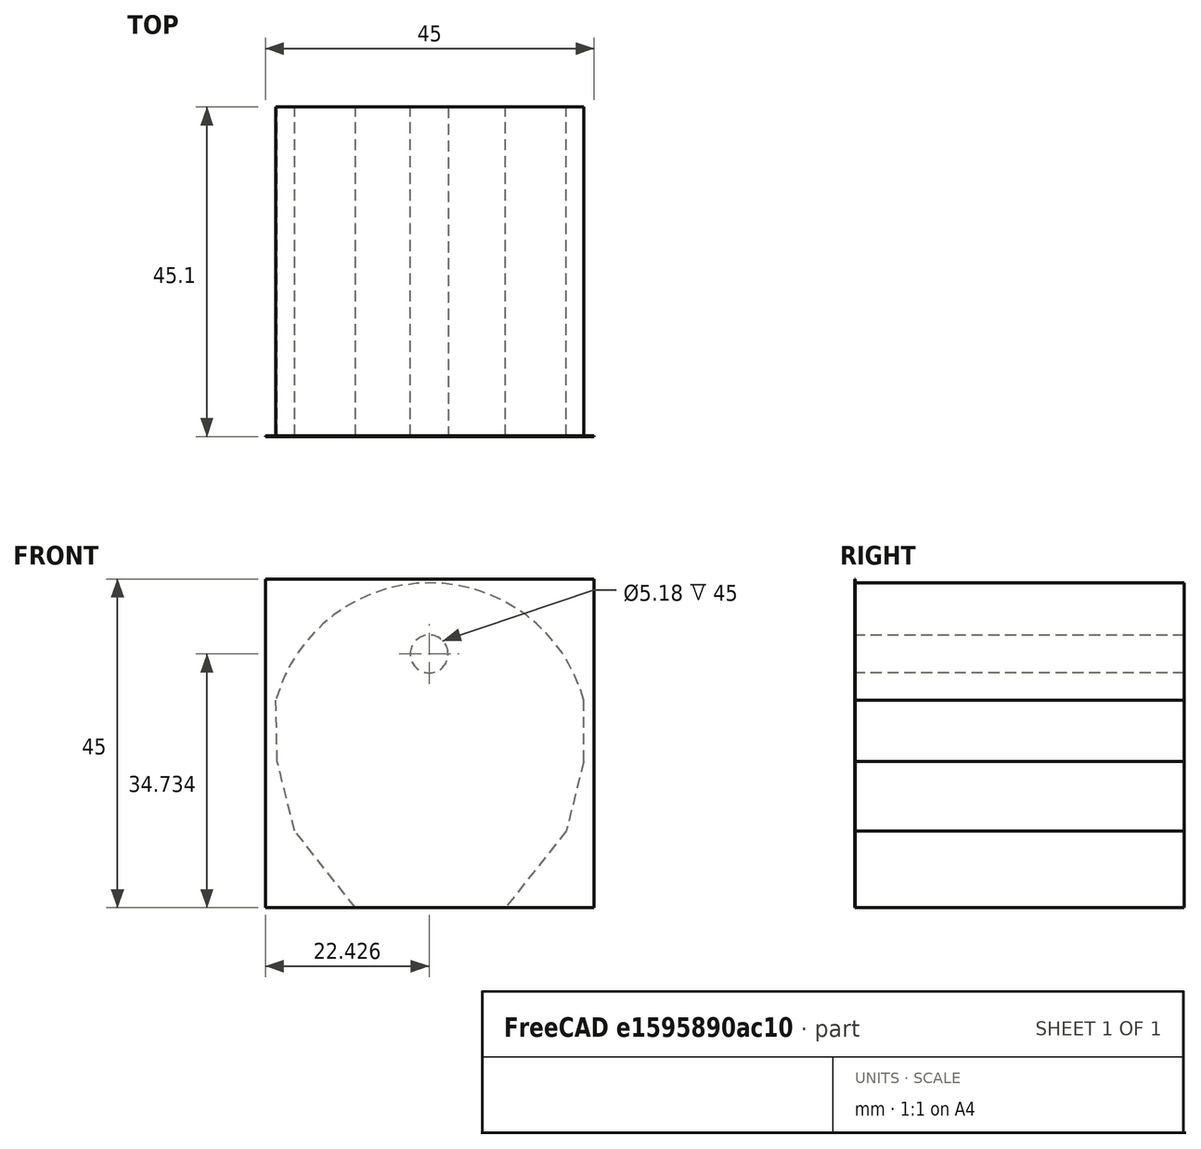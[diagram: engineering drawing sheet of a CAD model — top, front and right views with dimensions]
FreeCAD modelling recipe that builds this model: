
FCSTD DOCUMENT  (FreeCAD 0.16R6707 (Git))
Label: ironCabeza
License: All rights reserved
LicenseURL: http://en.wikipedia.org/wiki/All_rights_reserved
objects: Mesh::Feature×1, Part::Box×1, Sketcher::SketchObject×1, PartDesign::Pad×1
note: 4 computed .brp shape members not serialized (recipe doc carries the construction recipe); baked Part::Feature solids carry a one-line shape summary decoded from their .brp

FEATURE [Mesh::Feature] Iron_Man
  Placement = pos=(22,47,23) rot=(1,0,0;1.5708rad)
FEATURE [Part::Box] Box  label="Cubo"
  Height = 45
  Length = 45
  Width = 0.1
FEATURE [Sketcher::SketchObject] Sketch
  Placement = pos=(0,0.1,0) rot=(0,0.707107,0.707107;3.14159rad)
  Support = -> Box [Face4]
  sketch-geometry (12):
    g0: LineSegment StartX=-43.5843 StartY=20.0496 StartZ=0 EndX=-41.1908 EndY=10.5192 EndZ=0
    g1: LineSegment StartX=-32.8759 StartY=0 StartZ=0 EndX=-12.3384 EndY=0 EndZ=0
    g2: LineSegment StartX=-4.02355 StartY=10.5192 StartZ=0 EndX=-1.62997 EndY=20.0496 EndZ=0
    g3: LineSegment StartX=-43.5843 StartY=20.0496 StartZ=0 EndX=-43.5843 EndY=28.422 EndZ=0
    g4: LineSegment StartX=-1.62997 StartY=20.0496 StartZ=0 EndX=-1.45192 EndY=28.422 EndZ=0
    g5: ArcOfCircle CenterX=-22.5181 CenterY=22.613 CenterZ=0 NormalX=0 NormalY=0 NormalZ=1 Radius=21.8525 StartAngle=0.269064 EndAngle=2.87253
    g6: LineSegment StartX=-41.1908 StartY=10.5192 StartZ=0 EndX=-32.8759 EndY=0 EndZ=0
    g7: LineSegment StartX=-12.3384 StartY=0 StartZ=0 EndX=-4.02355 EndY=10.5192 EndZ=0
    g8: LineSegment [constr] StartX=-43.5843 StartY=28.422 StartZ=0 EndX=-1.45192 EndY=28.422 EndZ=0
    g9: LineSegment [constr] StartX=-41.1908 StartY=10.5192 StartZ=0 EndX=-4.02355 EndY=10.5192 EndZ=0
    g10: LineSegment [constr] StartX=-43.5843 StartY=20.0496 StartZ=0 EndX=-1.62997 EndY=20.0496 EndZ=0
    g11: Circle CenterX=-22.4258 CenterY=34.7344 CenterZ=0 NormalX=0 NormalY=0 NormalZ=1 Radius=2.59212
  constraints (22):
    c: Horizontal(g1)
    c: Vertical(g3)
    c: Coincident(g4,g2)
    c: Coincident(g5,g3)
    c: Coincident(g5,g4)
    c: Coincident(g6,g0)
    c: Coincident(g6,g1)
    c: Coincident(g7,g1)
    c: Coincident(g7,g2)
    c: Horizontal(g8)
    c: Coincident(g8,g3)
    c: Coincident(g8,g4)
    c: Coincident(g9,g0)
    c: Coincident(g9,g2)
    c: Horizontal(g9)
    c: Coincident(g10,g3)
    c: Coincident(g10,g2)
    c: Horizontal(g10)
    c: PointOnObject(g1,g-1)
    c: Coincident(g3,g0)
    c: Equal(g0,g2)
    c: Equal(g6,g7)
FEATURE [PartDesign::Pad] Pad
  Length = 45
  Length2 = 100
  Sketch = -> Sketch
  Type = 0
